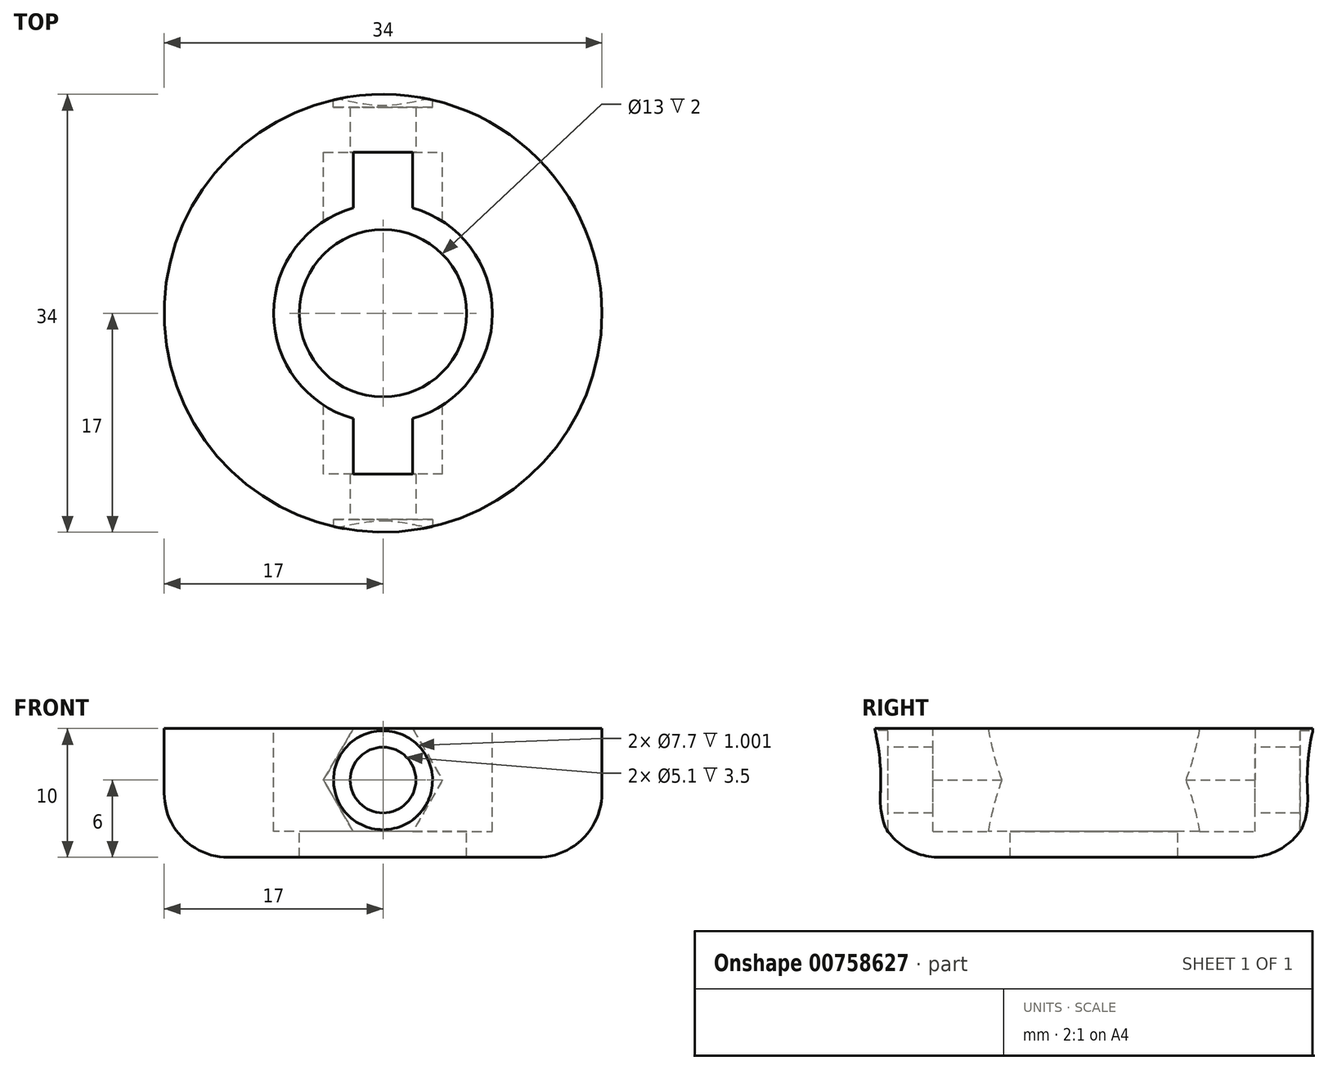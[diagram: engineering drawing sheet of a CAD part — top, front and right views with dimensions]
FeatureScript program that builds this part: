
annotation { "Feature Type Name" : "Feature", "Feature Type Description" : "" }
export const myFeature = defineFeature(function(context is Context, id is Id, definition is map)
    precondition{}
    {
        {
            var Q0;
            Q0=qCreatedBy(makeId("Top.planeOp"),FACE);
            var sketch = newSketch(context, id + "F0", { "sketchPlane" : qUnion([Q0])});
            skCircle(sketch, "E0", {"center": v(0, 0) * mm, "radius": 17 * mm});
            skSolve(sketch);
        }
        {
            var Q0;
            Q0=makeQuery(id+"F0.imprint","IMPRINT",FACE,{"disambiguationData":[TD([[makeQuery(id+"F0.imprint","IMPRINT",EDGE,{"derivedFrom":sQuery(id+"F0.wireOp",EDGE,"E0")}),1.0]])]});
            extrude(context, id + "F1", {"entities" : qUnion([Q0]), "depth" : 10 * mm, "offsetDistance" : 25 * mm});
        }
        {
            var Q0;
            Q0=makeQuery(id+"F1.opExtrude","CAP_FACE",FACE,{"disambiguationData":[OSD([sQuery(id+"F0.wireOp",EDGE,"E0")])],"isStart":false});
            var sketch = newSketch(context, id + "F2", { "sketchPlane" : qUnion([Q0])});
            skCircle(sketch, "E1", {"center": v(0, 0) * mm, "radius": 8.5 * mm});
            skSolve(sketch);
        }
        {
            var Q0;
            Q0=makeQuery(id+"F2.imprint","IMPRINT",FACE,{"disambiguationData":[TD([[makeQuery(id+"F2.imprint","IMPRINT",EDGE,{"derivedFrom":sQuery(id+"F2.wireOp",EDGE,"E1")}),1.0]])]});
            extrude(context, id + "F3", {"entities" : qUnion([Q0]), "operationType" : NewBodyOperationType.REMOVE, "oppositeDirection" : true, "depth" : 8 * mm, "offsetDistance" : 25 * mm});
        }
        {
            var Q0;
            Q0=makeQuery(id+"F3.boolean.opBoolean","COPY",FACE,{"derivedFrom":makeQuery(id+"F3.opExtrude","CAP_FACE",FACE,{"disambiguationData":[OSD([sQuery(id+"F2.wireOp",EDGE,"E1")])],"isStart":false})});
            var sketch = newSketch(context, id + "F4", { "sketchPlane" : qUnion([Q0])});
            skCircle(sketch, "E2", {"center": v(0, 0) * mm, "radius": 6.5 * mm});
            skSolve(sketch);
        }
        {
            var Q0;
            Q0=makeQuery(id+"F4.imprint","IMPRINT",FACE,{"disambiguationData":[TD([[makeQuery(id+"F4.imprint","IMPRINT",EDGE,{"derivedFrom":sQuery(id+"F4.wireOp",EDGE,"E2")}),1.0]])]});
            extrude(context, id + "F5", {"entities" : qUnion([Q0]), "operationType" : NewBodyOperationType.REMOVE, "endBound" : BoundingType.THROUGH_ALL, "oppositeDirection" : true, "depth" : 25 * mm, "offsetDistance" : 25 * mm});
        }
        {
            var Q0;
            Q0=qCreatedBy(makeId("Front.planeOp"),FACE);
            var sketch = newSketch(context, id + "F6", { "sketchPlane" : qUnion([Q0])});
            skCircle(sketch, "E3.cCircle", {"center": v(0, 6) * mm, "radius": 4 * mm, "construction": true});
            skLineSegment(sketch, "E3.0", {"start": v(2.3, 10) * mm, "end": v(4.62, 6) * mm});
            skLineSegment(sketch, "E3.1", {"start": v(4.62, 6) * mm, "end": v(2.3, 2) * mm});
            skLineSegment(sketch, "E3.2", {"start": v(2.3, 2) * mm, "end": v(-2.3, 2) * mm});
            skLineSegment(sketch, "E3.3", {"start": v(-2.3, 2) * mm, "end": v(-4.62, 6) * mm});
            skLineSegment(sketch, "E3.4", {"start": v(-4.62, 6) * mm, "end": v(-2.3, 10) * mm});
            skLineSegment(sketch, "E3.5", {"start": v(-2.3, 10) * mm, "end": v(2.3, 10) * mm});
            skPoint(sketch, "E3.0.midPoint", {"position": v(3.46, 8) * mm});
            skSolve(sketch);
        }
        {
            var Q0;
            Q0=makeQuery(id+"F6.imprint","IMPRINT",FACE,{"disambiguationData":[TD([[makeQuery(id+"F6.imprint","IMPRINT",EDGE,{"derivedFrom":sQuery(id+"F6.wireOp",EDGE,"E3.0")}),-1.0]])]});
            extrude(context, id + "F7", {"entities" : qUnion([Q0]), "operationType" : NewBodyOperationType.REMOVE, "depth" : 25 * mm, "offsetDistance" : 25 * mm, "hasSecondDirection" : true, "secondDirectionOppositeDirection" : true, "secondDirectionDepth" : 11.7 * mm, "symmetric" : true});
        }
        {
            var Q0;
            Q0=qCreatedBy(makeId("Front.planeOp"),FACE);
            cPlane(context, id + "F8", {"entities" : qUnion([Q0]), "cplaneType" : CPlaneType.OFFSET, "offset" : 17.5 * mm, "width" : 150 * mm, "height" : 150 * mm});
        }
        {
            var Q0;
            Q0=qCreatedBy(makeId("Front.planeOp"),FACE);
            cPlane(context, id + "F9", {"entities" : qUnion([Q0]), "cplaneType" : CPlaneType.OFFSET, "offset" : 17.5 * mm, "oppositeDirection" : true, "width" : 150 * mm, "height" : 150 * mm});
        }
        {
            var Q0;
            Q0=qCreatedBy(id+"F8.planeOp",FACE);
            var sketch = newSketch(context, id + "F10", { "sketchPlane" : qUnion([Q0])});
            skCircle(sketch, "E4", {"center": v(0, 6) * mm, "radius": 3.85 * mm});
            skSolve(sketch);
        }
        {
            var Q0;
            Q0 = qSketchRegion(id + "F10", true);
            extrude(context, id + "F11", {"entities" : qUnion([Q0]), "operationType" : NewBodyOperationType.REMOVE, "surfaceOperationType" : NewSurfaceOperationType.ADD, "oppositeDirection" : true, "depth" : 1.5 * mm, "offsetDistance" : 25 * mm});
        }
        {
            var Q0;
            Q0=qCreatedBy(id+"F9.planeOp",FACE);
            var sketch = newSketch(context, id + "F12", { "sketchPlane" : qUnion([Q0])});
            skCircle(sketch, "E5", {"center": v(0, 6) * mm, "radius": 3.85 * mm});
            skSolve(sketch);
        }
        {
            var Q0;
            Q0 = qSketchRegion(id + "F12", true);
            extrude(context, id + "F13", {"entities" : qUnion([Q0]), "operationType" : NewBodyOperationType.REMOVE, "depth" : 1.5 * mm, "offsetDistance" : 25 * mm});
        }
        {
            var Q0;
            Q0=makeQuery(id+"F1.opExtrude","CAP_EDGE",EDGE,{"disambiguationData":[OSD([sQuery(id+"F0.wireOp",EDGE,"E0")])],"isStart":true});
            fillet(context, id + "F14", {"entities" : qUnion([Q0]), "radius" : 5 * mm, "tangentPropagation" : true, "allowEdgeOverflow" : false});
        }
        {
            var Q0;
            Q0=qCreatedBy(id+"F8.planeOp",FACE);
            var sketch = newSketch(context, id + "F15", { "sketchPlane" : qUnion([Q0])});
            skCircle(sketch, "E6", {"center": v(0, 6) * mm, "radius": 2.55 * mm});
            skSolve(sketch);
        }
        {
            var Q0;
            Q0 = qSketchRegion(id + "F15", true);
            extrude(context, id + "F16", {"entities" : qUnion([Q0]), "operationType" : NewBodyOperationType.REMOVE, "endBound" : BoundingType.THROUGH_ALL, "oppositeDirection" : true, "depth" : 25 * mm, "offsetDistance" : 25 * mm});
        }
    });
